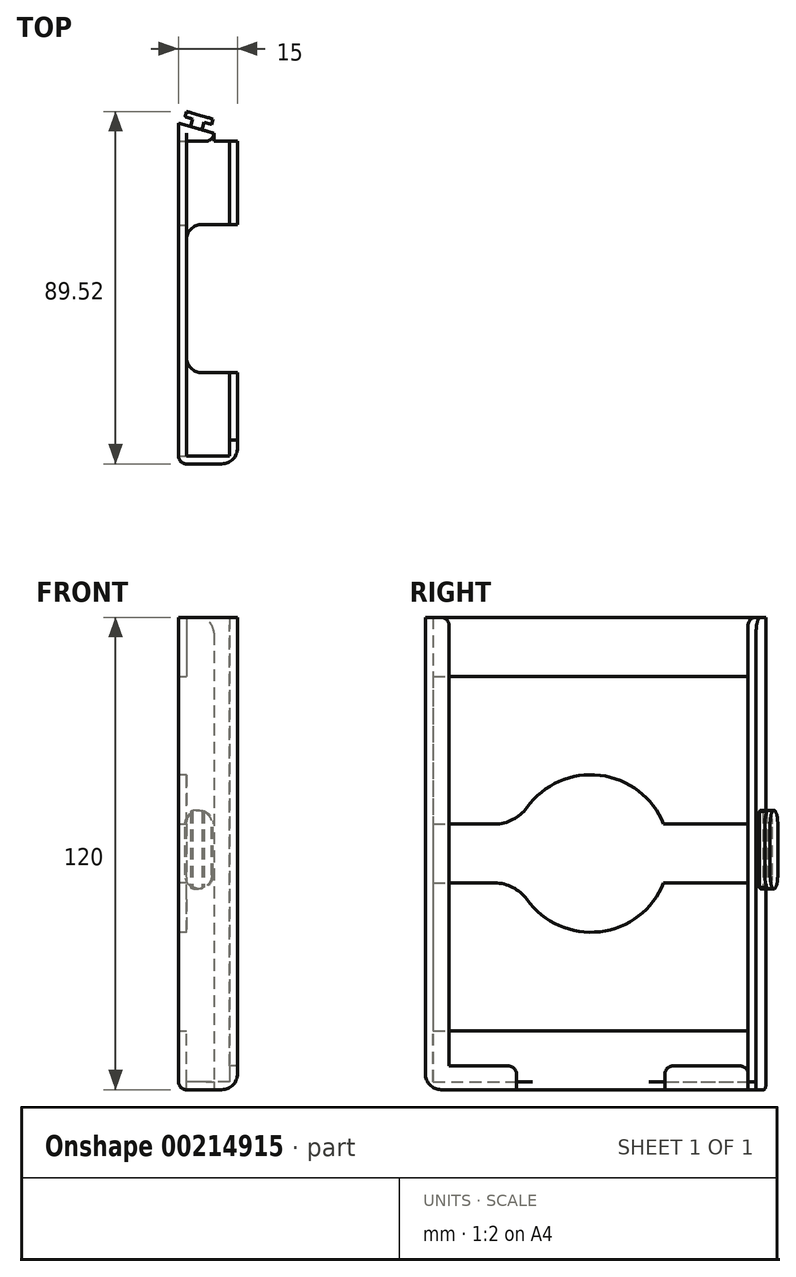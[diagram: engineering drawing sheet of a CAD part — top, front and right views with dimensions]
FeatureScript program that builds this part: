
annotation { "Feature Type Name" : "Feature", "Feature Type Description" : "" }
export const myFeature = defineFeature(function(context is Context, id is Id, definition is map)
    precondition{}
    {
        {
            var Q0;
            Q0=qCreatedBy(makeId("Front.planeOp"),FACE);
            var sketch = newSketch(context, id + "F0", { "sketchPlane" : qUnion([Q0])});
            skLineSegment(sketch, "E0.bottom", {"start": v(3.5, -10) * mm, "end": v(-3.5, -10) * mm});
            skLineSegment(sketch, "E0.top", {"start": v(3.5, 10) * mm, "end": v(-3.5, 10) * mm});
            skLineSegment(sketch, "E0.left", {"start": v(3.5, -10) * mm, "end": v(3.5, 10) * mm});
            skLineSegment(sketch, "E0.right", {"start": v(-3.5, -10) * mm, "end": v(-3.5, 10) * mm});
            skPoint(sketch, "E0.middle", {"position": v(0, 0) * mm});
            skSolve(sketch);
        }
        {
            var Q0;
            Q0=makeQuery(id+"F0.imprint","IMPRINT",FACE,{"disambiguationData":[TD([[makeQuery(id+"F0.imprint","IMPRINT",EDGE,{"derivedFrom":sQuery(id+"F0.wireOp",EDGE,"E0.bottom")}),-1.0]])]});
            extrude(context, id + "F1", {"entities" : qUnion([Q0]), "depth" : 1.4 * mm});
        }
        {
            var Q0;
            Q0=qCreatedBy(makeId("Front.planeOp"),FACE);
            var sketch = newSketch(context, id + "F2", { "sketchPlane" : qUnion([Q0])});
            skLineSegment(sketch, "E1.bottom", {"start": v(5.5, 60) * mm, "end": v(-3.5, 60) * mm});
            skLineSegment(sketch, "E1.top", {"start": v(5.5, -60) * mm, "end": v(-3.5, -60) * mm});
            skLineSegment(sketch, "E1.left", {"start": v(5.5, 60) * mm, "end": v(5.5, -60) * mm});
            skLineSegment(sketch, "E1.right", {"start": v(-3.5, 60) * mm, "end": v(-3.5, -60) * mm});
            skPoint(sketch, "E1.middle", {"position": v(1, 0) * mm});
            skSolve(sketch);
        }
        {
            var Q0;
            Q0=qSketchRegion(id+"F2",true);
            extrude(context, id + "F3", {"entities" : qUnion([Q0]), "operationType" : NewBodyOperationType.ADD, "depth" : 2 * mm});
        }
        {
            var Q0;
            Q0=makeQuery(id+"F11.boolean.opBoolean","MERGE",FACE,{"derivedFrom":[makeQuery(id+"F9.boolean.opBoolean","MERGE",FACE,{"derivedFrom":[makeQuery(id+"F7.boolean.opBoolean","MERGE",FACE,{"derivedFrom":[makeQuery(id+"F3.opExtrude","SWEPT_FACE",FACE,{"disambiguationData":[OSD([sQuery(id+"F2.wireOp",EDGE,"E1.top")])]}),makeQuery(id+"F7.opExtrude","SWEPT_FACE",FACE,{"disambiguationData":[OSD([sQuery(id+"F6.wireOp",EDGE,"E5.bottom")])]})]}),makeQuery(id+"F9.opExtrude","SWEPT_FACE",FACE,{"disambiguationData":[OSD([sQuery(id+"F8.wireOp",EDGE,"E8.top")])]})]}),makeQuery(id+"F11.opExtrude","SWEPT_FACE",FACE,{"disambiguationData":[OSD([sQuery(id+"F10.wireOp",EDGE,"E9.bottom")])]})]});
            var sketch = newSketch(context, id + "F4", { "sketchPlane" : qUnion([Q0])});
            skLineSegment(sketch, "E2", {"start": v(5.5, 0) * mm, "end": v(-3.5, -2.58) * mm});
            skLineSegment(sketch, "E3", {"start": v(-3.5, -2.58) * mm, "end": v(-3.5, 0) * mm});
            skSolve(sketch);
        }
        {
            var Q0;
            Q0 = qSketchRegion(id + "F4", true);
            var Q1;
            Q1=makeQuery(id+"F4.imprint","IMPRINT",FACE,{"disambiguationData":[TD([[makeQuery(id+"F4.imprint","IMPRINT",EDGE,{"derivedFrom":sQuery(id+"F4.wireOp",EDGE,"E2")}),-1.0]])]});
            var Q2;
            Q2=makeQuery(id+"F3.opExtrude","CAP_VERTEX",VERTEX,{"disambiguationData":[OSD([sQuery(id+"F2.wireOp",EDGE,"E1.bottom"),sQuery(id+"F2.wireOp",EDGE,"E1.right")])],"isStart":true});
            extrude(context, id + "F5", {"entities" : qUnion([Q0, Q1]), "operationType" : NewBodyOperationType.ADD, "endBound" : BoundingType.UP_TO_VERTEX, "oppositeDirection" : true, "endBoundEntityVertex" : qUnion([Q2]), "depth" : 25 * mm});
        }
        {
            var Q0;
            Q0=makeQuery(id+"F3.opExtrude","CAP_FACE",FACE,{"disambiguationData":[OSD([sQuery(id+"F2.wireOp",EDGE,"E1.bottom"),sQuery(id+"F2.wireOp",EDGE,"E1.top"),sQuery(id+"F2.wireOp",EDGE,"E1.left"),sQuery(id+"F2.wireOp",EDGE,"E1.right")])],"isStart":false});
            var sketch = newSketch(context, id + "F6", { "sketchPlane" : qUnion([Q0])});
            skLineSegment(sketch, "E4.bottom", {"start": v(-3.5, 60) * mm, "end": v(-1.5, 60) * mm});
            skLineSegment(sketch, "E4.top", {"start": v(-3.5, 45) * mm, "end": v(-1.5, 45) * mm});
            skLineSegment(sketch, "E4.left", {"start": v(-3.5, 60) * mm, "end": v(-3.5, 45) * mm});
            skLineSegment(sketch, "E4.right", {"start": v(-1.5, 60) * mm, "end": v(-1.5, 45) * mm});
            skLineSegment(sketch, "E5.bottom", {"start": v(-3.5, -60) * mm, "end": v(-1.5, -60) * mm});
            skLineSegment(sketch, "E5.top", {"start": v(-3.5, -45) * mm, "end": v(-1.5, -45) * mm});
            skLineSegment(sketch, "E5.left", {"start": v(-3.5, -60) * mm, "end": v(-3.5, -45) * mm});
            skLineSegment(sketch, "E5.right", {"start": v(-1.5, -60) * mm, "end": v(-1.5, -45) * mm});
            skLineSegment(sketch, "E6.bottom", {"start": v(-3.5, 7.5) * mm, "end": v(-1.5, 7.5) * mm});
            skLineSegment(sketch, "E6.top", {"start": v(-3.5, -7.5) * mm, "end": v(-1.5, -7.5) * mm});
            skLineSegment(sketch, "E6.left", {"start": v(-3.5, 7.5) * mm, "end": v(-3.5, -7.5) * mm});
            skLineSegment(sketch, "E6.right", {"start": v(-1.5, 7.5) * mm, "end": v(-1.5, -7.5) * mm});
            skPoint(sketch, "E7", {"position": v(-3.5, 0) * mm});
            skSolve(sketch);
        }
        {
            var Q0;
            Q0=qSketchRegion(id+"F6",true);
            extrude(context, id + "F7", {"entities" : qUnion([Q0]), "operationType" : NewBodyOperationType.ADD, "depth" : 80 * mm});
        }
        {
            var Q0;
            Q0=makeQuery(id+"F7.opExtrude","CAP_FACE",FACE,{"disambiguationData":[OSD([sQuery(id+"F6.wireOp",EDGE,"E4.bottom"),sQuery(id+"F6.wireOp",EDGE,"E4.top"),sQuery(id+"F6.wireOp",EDGE,"E4.left"),sQuery(id+"F6.wireOp",EDGE,"E4.right")])],"isStart":false});
            var sketch = newSketch(context, id + "F8", { "sketchPlane" : qUnion([Q0])});
            skLineSegment(sketch, "E8.bottom", {"start": v(-3.5, 60) * mm, "end": v(11.5, 60) * mm});
            skLineSegment(sketch, "E8.top", {"start": v(-3.5, -60) * mm, "end": v(11.5, -60) * mm});
            skLineSegment(sketch, "E8.left", {"start": v(-3.5, 60) * mm, "end": v(-3.5, -60) * mm});
            skLineSegment(sketch, "E8.right", {"start": v(11.5, 60) * mm, "end": v(11.5, -60) * mm});
            skSolve(sketch);
        }
        {
            var Q0;
            {var subQ2=sQuery(id+"F8.wireOp",EDGE,"E8.top");Q0=makeQuery(id+"F8.imprint","IMPRINT",FACE,{"disambiguationData":[TD([[makeQuery(id+"F8.imprint","IMPRINT",EDGE,{"derivedFrom":subQ2}),1.0]])]});}
            var Q1;
            {var subQ4=makeQuery(id+"F7.opExtrude","CAP_EDGE",EDGE,{"disambiguationData":[OSD([sQuery(id+"F6.wireOp",EDGE,"E4.top")])],"isStart":false});Q1=makeQuery(id+"F8.imprint","IMPRINT",FACE,{"disambiguationData":[TD([[makeQuery(id+"F8.imprint","IMPRINT",EDGE,{"derivedFrom":subQ4}),1.0]])]});}
            extrude(context, id + "F9", {"entities" : qUnion([Q0, Q1]), "operationType" : NewBodyOperationType.ADD, "depth" : 2 * mm});
        }
        {
            var Q0;
            Q0=makeQuery(id+"F7.opExtrude","SWEPT_FACE",FACE,{"disambiguationData":[OSD([sQuery(id+"F6.wireOp",EDGE,"E5.right")])]});
            var sketch = newSketch(context, id + "F10", { "sketchPlane" : qUnion([Q0])});
            skLineSegment(sketch, "E9.bottom", {"start": v(-82, -60) * mm, "end": v(-2, -60) * mm});
            skLineSegment(sketch, "E9.top", {"start": v(-82, -58) * mm, "end": v(-2, -58) * mm});
            skLineSegment(sketch, "E9.left", {"start": v(-82, -60) * mm, "end": v(-82, -58) * mm});
            skLineSegment(sketch, "E9.right", {"start": v(-2, -60) * mm, "end": v(-2, -58) * mm});
            skSolve(sketch);
        }
        {
            var Q0;
            Q0=makeQuery(id+"F10.imprint","IMPRINT",FACE,{"disambiguationData":[TD([[makeQuery(id+"F10.imprint","IMPRINT",EDGE,{"derivedFrom":sQuery(id+"F10.wireOp",EDGE,"E9.bottom")}),1.0]])]});
            var Q1;
            Q1=makeQuery(id+"F9.opExtrude","CAP_VERTEX",VERTEX,{"disambiguationData":[OSD([sQuery(id+"F8.wireOp",EDGE,"E8.top"),sQuery(id+"F8.wireOp",EDGE,"E8.right")])],"isStart":true});
            extrude(context, id + "F11", {"entities" : qUnion([Q0]), "operationType" : NewBodyOperationType.ADD, "endBound" : BoundingType.UP_TO_VERTEX, "endBoundEntityVertex" : qUnion([Q1]), "depth" : 25 * mm});
        }
        {
            var Q0;
            Q0=makeQuery(id+"F11.opExtrude","SWEPT_FACE",FACE,{"disambiguationData":[OSD([sQuery(id+"F10.wireOp",EDGE,"E9.top")])]});
            var sketch = newSketch(context, id + "F12", { "sketchPlane" : qUnion([Q0])});
            skLineSegment(sketch, "E10.bottom", {"start": v(11.5, -23.15) * mm, "end": v(-1.5, -23.15) * mm});
            skLineSegment(sketch, "E10.top", {"start": v(11.5, -60.85) * mm, "end": v(-1.5, -60.85) * mm});
            skLineSegment(sketch, "E10.left", {"start": v(11.5, -23.15) * mm, "end": v(11.5, -60.85) * mm});
            skLineSegment(sketch, "E10.right", {"start": v(-1.5, -23.15) * mm, "end": v(-1.5, -60.85) * mm});
            skPoint(sketch, "E10.middle", {"position": v(5, -42) * mm});
            skPoint(sketch, "E10.middle.positionSnap0", {"position": v(5, -82) * mm});
            skPoint(sketch, "E10.middle.positionSnap1", {"position": v(-1.5, -42) * mm});
            skPoint(sketch, "E10.centerSnap0", {"position": v(5, -82) * mm});
            skPoint(sketch, "E10.centerSnap1", {"position": v(-1.5, -42) * mm});
            skSolve(sketch);
        }
        {
            var Q0;
            Q0=makeQuery(id+"F12.imprint","IMPRINT",FACE,{"disambiguationData":[TD([[makeQuery(id+"F12.imprint","IMPRINT",EDGE,{"derivedFrom":sQuery(id+"F12.wireOp",EDGE,"E10.bottom")}),1.0]])]});
            extrude(context, id + "F13", {"entities" : qUnion([Q0]), "operationType" : NewBodyOperationType.REMOVE, "endBound" : BoundingType.THROUGH_ALL, "oppositeDirection" : true, "depth" : 25 * mm});
        }
        {
            var Q0;
            Q0=makeQuery(id+"F13.boolean.opBoolean","SPLIT",FACE,{"disambiguationData":[TD([makeQuery(id+"F13.opExtrude","SWEPT_FACE",FACE,{"disambiguationData":[OSD([sQuery(id+"F12.wireOp",EDGE,"E10.top")])]})])],"derivedFrom":makeQuery(id+"F11.opExtrude","SWEPT_FACE",FACE,{"disambiguationData":[OSD([sQuery(id+"F10.wireOp",EDGE,"E9.top")])]})});
            var sketch = newSketch(context, id + "F14", { "sketchPlane" : qUnion([Q0])});
            skLineSegment(sketch, "E11.bottom", {"start": v(11.5, -82) * mm, "end": v(9.5, -82) * mm});
            skLineSegment(sketch, "E11.top", {"start": v(11.5, -60.85) * mm, "end": v(9.5, -60.85) * mm});
            skLineSegment(sketch, "E11.left", {"start": v(11.5, -82) * mm, "end": v(11.5, -60.85) * mm});
            skLineSegment(sketch, "E11.right", {"start": v(9.5, -82) * mm, "end": v(9.5, -60.85) * mm});
            skSolve(sketch);
        }
        {
            var Q0;
            {var subQ0=sQuery(id+"F2.wireOp",EDGE,"E1.left");Q0=makeQuery(id+"F13.boolean.opBoolean","SPLIT",FACE,{"disambiguationData":[TD([makeQuery(id+"F3.opExtrude","SWEPT_FACE",FACE,{"disambiguationData":[OSD([subQ0])]})])],"derivedFrom":makeQuery(id+"F11.opExtrude","SWEPT_FACE",FACE,{"disambiguationData":[OSD([sQuery(id+"F10.wireOp",EDGE,"E9.top")])]})});}
            var sketch = newSketch(context, id + "F15", { "sketchPlane" : qUnion([Q0])});
            skLineSegment(sketch, "E12.bottom", {"start": v(11.5, -23.15) * mm, "end": v(9.5, -23.15) * mm});
            skLineSegment(sketch, "E12.top", {"start": v(11.5, -2) * mm, "end": v(9.5, -2) * mm});
            skLineSegment(sketch, "E12.left", {"start": v(11.5, -23.15) * mm, "end": v(11.5, -2) * mm});
            skLineSegment(sketch, "E12.right", {"start": v(9.5, -23.15) * mm, "end": v(9.5, -2) * mm});
            skSolve(sketch);
        }
        {
            var Q0;
            Q0=makeQuery(id+"F14.imprint","IMPRINT",FACE,{"disambiguationData":[TD([[makeQuery(id+"F14.imprint","IMPRINT",EDGE,{"derivedFrom":sQuery(id+"F14.wireOp",EDGE,"E11.bottom")}),-1.0]])]});
            var Q1;
            Q1=makeQuery(id+"F15.imprint","IMPRINT",FACE,{"disambiguationData":[TD([[makeQuery(id+"F15.imprint","IMPRINT",EDGE,{"derivedFrom":sQuery(id+"F15.wireOp",EDGE,"E12.bottom")}),-1.0]])]});
            extrude(context, id + "F16", {"entities" : qUnion([Q0, Q1]), "operationType" : NewBodyOperationType.ADD, "depth" : 4 * mm});
        }
        {
            var Q0;
            Q0=makeQuery(id+"F9.opExtrude","CAP_FACE",FACE,{"disambiguationData":[OSD([sQuery(id+"F8.wireOp",EDGE,"E8.bottom"),sQuery(id+"F8.wireOp",EDGE,"E8.top"),sQuery(id+"F8.wireOp",EDGE,"E8.left"),sQuery(id+"F8.wireOp",EDGE,"E8.right")])],"isStart":true});
            var sketch = newSketch(context, id + "F17", { "sketchPlane" : qUnion([Q0])});
            skLineSegment(sketch, "E13.bottom", {"start": v(-11.5, -54) * mm, "end": v(-9.5, -54) * mm});
            skLineSegment(sketch, "E13.top", {"start": v(-11.5, 60) * mm, "end": v(-9.5, 60) * mm});
            skLineSegment(sketch, "E13.left", {"start": v(-11.5, -54) * mm, "end": v(-11.5, 60) * mm});
            skLineSegment(sketch, "E13.right", {"start": v(-9.5, -54) * mm, "end": v(-9.5, 60) * mm});
            skSolve(sketch);
        }
        {
            var Q0;
            Q0=makeQuery(id+"F17.imprint","IMPRINT",FACE,{"disambiguationData":[TD([[makeQuery(id+"F17.imprint","IMPRINT",EDGE,{"derivedFrom":sQuery(id+"F17.wireOp",EDGE,"E13.bottom")}),1.0]])]});
            extrude(context, id + "F18", {"entities" : qUnion([Q0]), "operationType" : NewBodyOperationType.ADD, "depth" : 4 * mm});
        }
        {
            var Q0;
            {var subQ0=sQuery(id+"F8.wireOp",EDGE,"E8.right");var subQ1=dummyQuery(id+"F11.vertexPlane.planeOp",FACE);var subQ2=sQuery(id+"F8.wireOp",EDGE,"E8.top");var subQ3=sQuery(id+"F10.wireOp",EDGE,"E9.bottom");Q0=makeQuery(id+"F13.boolean.opBoolean","SPLIT",EDGE,{"disambiguationData":[TD([makeQuery(id+"F11.opExtrude","SWEPT_FACE",FACE,{"disambiguationData":[OSD([sQuery(id+"F10.wireOp",EDGE,"E9.right")])]})])],"derivedFrom":makeQuery(id+"F11.boolean.opBoolean","MERGE",EDGE,{"derivedFrom":[makeQuery(id+"F9.opExtrude","SWEPT_EDGE",EDGE,{"disambiguationData":[OSD([subQ2,subQ0])]}),makeQuery(id+"F11.opExtrude","TWEAK_EDGE",EDGE,{"derivedFrom":[makeQuery(id+"F10.imprint","IMPRINT",EDGE,{"derivedFrom":subQ3}),subQ1]})]})});}
            var Q1;
            {var subQ0=sQuery(id+"F8.wireOp",EDGE,"E8.top");var subQ1=sQuery(id+"F10.wireOp",EDGE,"E9.bottom");var subQ2=sQuery(id+"F8.wireOp",EDGE,"E8.right");var subQ3=dummyQuery(id+"F11.vertexPlane.planeOp",FACE);Q1=makeQuery(id+"F13.boolean.opBoolean","SPLIT",EDGE,{"disambiguationData":[TD([makeQuery(id+"F13.opExtrude","SWEPT_FACE",FACE,{"disambiguationData":[OSD([sQuery(id+"F12.wireOp",EDGE,"E10.top")])]})])],"derivedFrom":makeQuery(id+"F11.boolean.opBoolean","MERGE",EDGE,{"derivedFrom":[makeQuery(id+"F9.opExtrude","SWEPT_EDGE",EDGE,{"disambiguationData":[OSD([subQ0,subQ2])]}),makeQuery(id+"F11.opExtrude","TWEAK_EDGE",EDGE,{"derivedFrom":[makeQuery(id+"F10.imprint","IMPRINT",EDGE,{"derivedFrom":subQ1}),subQ3]})]})});}
            var Q2;
            Q2=makeQuery(id+"F9.opExtrude","CAP_EDGE",EDGE,{"disambiguationData":[OSD([sQuery(id+"F8.wireOp",EDGE,"E8.right")])],"isStart":false});
            var Q3;
            Q3=makeQuery(id+"F16.opExtrude","CAP_EDGE",EDGE,{"disambiguationData":[OSD([sQuery(id+"F14.wireOp",EDGE,"E11.right")])],"isStart":true});
            var Q4;
            Q4=makeQuery(id+"F18.boolean.opBoolean","MERGE",EDGE,{"derivedFrom":[makeQuery(id+"F16.opExtrude","SWEPT_EDGE",EDGE,{"disambiguationData":[OSD([sQuery(id+"F6.wireOp",EDGE,"E5.right"),sQuery(id+"F10.wireOp",EDGE,"E9.top"),sQuery(id+"F10.wireOp",EDGE,"E9.left"),sQuery(id+"F14.wireOp",EDGE,"E11.bottom"),sQuery(id+"F14.wireOp",EDGE,"E11.right")])]}),makeQuery(id+"F18.opExtrude","CAP_EDGE",EDGE,{"disambiguationData":[OSD([sQuery(id+"F17.wireOp",EDGE,"E13.right")])],"isStart":true})]});
            var Q5;
            Q5=makeQuery(id+"F16.opExtrude","CAP_EDGE",EDGE,{"disambiguationData":[OSD([sQuery(id+"F15.wireOp",EDGE,"E12.right")])],"isStart":true});
            var Q6;
            Q6=makeQuery(id+"F3.opExtrude","SWEPT_EDGE",EDGE,{"disambiguationData":[OSD([sQuery(id+"F2.wireOp",EDGE,"E1.bottom"),sQuery(id+"F2.wireOp",EDGE,"E1.left")])]});
            var Q7;
            Q7=makeQuery(id+"F9.opExtrude","CAP_EDGE",EDGE,{"disambiguationData":[OSD([sQuery(id+"F8.wireOp",EDGE,"E8.top")])],"isStart":false});
            var Q8;
            Q8=makeQuery(id+"F11.opExtrude","SWEPT_EDGE",EDGE,{"disambiguationData":[OSD([sQuery(id+"F6.wireOp",EDGE,"E5.right"),sQuery(id+"F10.wireOp",EDGE,"E9.top"),sQuery(id+"F10.wireOp",EDGE,"E9.left")])]});
            var Q9;
            Q9=makeQuery(id+"F13.boolean.opBoolean","COPY",EDGE,{"derivedFrom":makeQuery(id+"F13.opExtrude","SWEPT_EDGE",EDGE,{"disambiguationData":[OSD([sQuery(id+"F10.wireOp",EDGE,"E9.top"),sQuery(id+"F12.wireOp",EDGE,"E10.bottom"),sQuery(id+"F12.wireOp",EDGE,"E10.right")])]})});
            var Q10;
            Q10=makeQuery(id+"F13.boolean.opBoolean","COPY",EDGE,{"derivedFrom":makeQuery(id+"F13.opExtrude","SWEPT_EDGE",EDGE,{"disambiguationData":[OSD([sQuery(id+"F10.wireOp",EDGE,"E9.top"),sQuery(id+"F12.wireOp",EDGE,"E10.top"),sQuery(id+"F12.wireOp",EDGE,"E10.right")])]})});
            var Q11;
            Q11=makeQuery(id+"F7.opExtrude","CAP_EDGE",EDGE,{"disambiguationData":[OSD([sQuery(id+"F6.wireOp",EDGE,"E6.top")])],"isStart":true});
            var Q12;
            Q12=makeQuery(id+"F7.opExtrude","CAP_EDGE",EDGE,{"disambiguationData":[OSD([sQuery(id+"F6.wireOp",EDGE,"E6.top")])],"isStart":false});
            var Q13;
            Q13=makeQuery(id+"F7.opExtrude","CAP_EDGE",EDGE,{"disambiguationData":[OSD([sQuery(id+"F6.wireOp",EDGE,"E5.top")])],"isStart":false});
            var Q14;
            Q14=makeQuery(id+"F7.opExtrude","CAP_EDGE",EDGE,{"disambiguationData":[OSD([sQuery(id+"F6.wireOp",EDGE,"E5.top")])],"isStart":true});
            var Q15;
            Q15=makeQuery(id+"F7.opExtrude","CAP_EDGE",EDGE,{"disambiguationData":[OSD([sQuery(id+"F6.wireOp",EDGE,"E4.top")])],"isStart":false});
            var Q16;
            Q16=makeQuery(id+"F7.opExtrude","CAP_EDGE",EDGE,{"disambiguationData":[OSD([sQuery(id+"F6.wireOp",EDGE,"E4.top")])],"isStart":true});
            var Q17;
            Q17=makeQuery(id+"F7.opExtrude","CAP_EDGE",EDGE,{"disambiguationData":[OSD([sQuery(id+"F6.wireOp",EDGE,"E6.bottom")])],"isStart":false});
            var Q18;
            Q18=makeQuery(id+"F7.opExtrude","CAP_EDGE",EDGE,{"disambiguationData":[OSD([sQuery(id+"F6.wireOp",EDGE,"E6.bottom")])],"isStart":true});
            fillet(context, id + "F19", {"entities" : qUnion([Q0, Q1, Q2, Q3, Q4, Q5, Q6, Q7, Q8, Q9, Q10, Q11, Q12, Q13, Q14, Q15, Q16, Q17, Q18]), "radius" : 4 * mm, "tangentPropagation" : true, "allowEdgeOverflow" : false});
        }
        {
            var Q0;
            {var subQ0=sQuery(id+"F2.wireOp",EDGE,"E1.top");var subQ1=sQuery(id+"F2.wireOp",EDGE,"E1.left");Q0=makeQuery(id+"F11.boolean.opBoolean","SPLIT",EDGE,{"disambiguationData":[TD([makeQuery(id+"F3.opExtrude","SWEPT_FACE",FACE,{"disambiguationData":[OSD([subQ0])]})])],"derivedFrom":makeQuery(id+"F3.opExtrude","CAP_EDGE",EDGE,{"disambiguationData":[OSD([subQ1])],"isStart":false})});}
            var Q1;
            Q1=makeQuery(id+"F16.opExtrude","CAP_EDGE",EDGE,{"disambiguationData":[OSD([sQuery(id+"F15.wireOp",EDGE,"E12.bottom")])],"isStart":false});
            var Q2;
            Q2=makeQuery(id+"F16.opExtrude","CAP_EDGE",EDGE,{"disambiguationData":[OSD([sQuery(id+"F15.wireOp",EDGE,"E12.top")])],"isStart":false});
            var Q3;
            Q3=makeQuery(id+"F16.opExtrude","CAP_EDGE",EDGE,{"disambiguationData":[OSD([sQuery(id+"F14.wireOp",EDGE,"E11.top")])],"isStart":false});
            var Q4;
            Q4=makeQuery(id+"F18.opExtrude","CAP_EDGE",EDGE,{"disambiguationData":[OSD([sQuery(id+"F17.wireOp",EDGE,"E13.bottom")])],"isStart":false});
            var Q5;
            Q5=makeQuery(id+"F18.opExtrude","CAP_EDGE",EDGE,{"disambiguationData":[OSD([sQuery(id+"F17.wireOp",EDGE,"E13.top")])],"isStart":false});
            var Q6;
            Q6=makeQuery(id+"F7.opExtrude","CAP_EDGE",EDGE,{"disambiguationData":[OSD([sQuery(id+"F6.wireOp",EDGE,"E4.right")])],"isStart":false});
            var Q7;
            Q7=makeQuery(id+"F7.opExtrude","CAP_EDGE",EDGE,{"disambiguationData":[OSD([sQuery(id+"F6.wireOp",EDGE,"E6.right")])],"isStart":false});
            var Q8;
            Q8=makeQuery(id+"F7.opExtrude","CAP_EDGE",EDGE,{"disambiguationData":[OSD([sQuery(id+"F6.wireOp",EDGE,"E5.right")])],"isStart":false});
            var Q9;
            {var subQ0=sQuery(id+"F10.wireOp",EDGE,"E9.top");Q9=makeQuery(id+"F13.boolean.opBoolean","SPLIT",EDGE,{"disambiguationData":[TD([makeQuery(id+"F13.opExtrude","SWEPT_FACE",FACE,{"disambiguationData":[OSD([sQuery(id+"F12.wireOp",EDGE,"E10.bottom")])]})])],"derivedFrom":makeQuery(id+"F11.opExtrude","CAP_EDGE",EDGE,{"disambiguationData":[OSD([subQ0])],"isStart":true})});}
            var Q10;
            Q10=makeQuery(id+"F7.opExtrude","CAP_EDGE",EDGE,{"disambiguationData":[OSD([sQuery(id+"F6.wireOp",EDGE,"E5.right")])],"isStart":true});
            var Q11;
            Q11=makeQuery(id+"F7.opExtrude","CAP_EDGE",EDGE,{"disambiguationData":[OSD([sQuery(id+"F6.wireOp",EDGE,"E6.right")])],"isStart":true});
            var Q12;
            Q12=makeQuery(id+"F7.opExtrude","CAP_EDGE",EDGE,{"disambiguationData":[OSD([sQuery(id+"F6.wireOp",EDGE,"E4.right")])],"isStart":true});
            var Q13;
            Q13=makeQuery(id+"F9.opExtrude","CAP_EDGE",EDGE,{"disambiguationData":[OSD([sQuery(id+"F8.wireOp",EDGE,"E8.left")])],"isStart":false});
            fillet(context, id + "F20", {"entities" : qUnion([Q0, Q1, Q2, Q3, Q4, Q5, Q6, Q7, Q8, Q9, Q10, Q11, Q12, Q13]), "radius" : 2 * mm, "tangentPropagation" : true, "allowEdgeOverflow" : false});
        }
        {
            var Q0;
            Q0=makeQuery(id+"F5.opExtrude","SWEPT_FACE",FACE,{"disambiguationData":[OSD([sQuery(id+"F4.wireOp",EDGE,"E2")])]});
            var sketch = newSketch(context, id + "F21", { "sketchPlane" : qUnion([Q0])});
            skLineSegment(sketch, "E14.bottom", {"start": v(0.9, 11) * mm, "end": v(-2.1, 11) * mm});
            skLineSegment(sketch, "E14.top", {"start": v(0.9, -9) * mm, "end": v(-2.1, -9) * mm});
            skLineSegment(sketch, "E14.left", {"start": v(0.9, 11) * mm, "end": v(0.9, -9) * mm});
            skLineSegment(sketch, "E14.right", {"start": v(-2.1, 11) * mm, "end": v(-2.1, -9) * mm});
            skPoint(sketch, "E14.middle", {"position": v(-0.6, 1) * mm});
            skLineSegment(sketch, "E15", {"start": v(4.08, 1) * mm, "end": v(-5.29, 1) * mm, "construction": true});
            skPoint(sketch, "E15.endSnap0", {"position": v(-5.29, -1) * mm});
            skSolve(sketch);
        }
        {
            var Q0;
            Q0=makeQuery(id+"F21.imprint","IMPRINT",FACE,{"disambiguationData":[TD([[makeQuery(id+"F21.imprint","IMPRINT",EDGE,{"derivedFrom":sQuery(id+"F21.wireOp",EDGE,"E14.bottom")}),1.0]])]});
            extrude(context, id + "F22", {"entities" : qUnion([Q0]), "operationType" : NewBodyOperationType.ADD, "depth" : 2 * mm});
        }
        {
            var Q0;
            Q0=makeQuery(id+"F22.opExtrude","CAP_FACE",FACE,{"disambiguationData":[OSD([sQuery(id+"F21.wireOp",EDGE,"E14.bottom"),sQuery(id+"F21.wireOp",EDGE,"E14.top"),sQuery(id+"F21.wireOp",EDGE,"E14.left"),sQuery(id+"F21.wireOp",EDGE,"E14.right")])],"isStart":false});
            var sketch = newSketch(context, id + "F23", { "sketchPlane" : qUnion([Q0])});
            skLineSegment(sketch, "E16.bottom", {"start": v(2.9, -9) * mm, "end": v(-4.1, -9) * mm});
            skLineSegment(sketch, "E16.top", {"start": v(2.9, 11) * mm, "end": v(-4.1, 11) * mm});
            skLineSegment(sketch, "E16.left", {"start": v(2.9, -9) * mm, "end": v(2.9, 11) * mm});
            skLineSegment(sketch, "E16.right", {"start": v(-4.1, -9) * mm, "end": v(-4.1, 11) * mm});
            skPoint(sketch, "E16.middle", {"position": v(-0.6, 1) * mm});
            skLineSegment(sketch, "E17", {"start": v(0.9, 1) * mm, "end": v(-2.1, 1) * mm, "construction": true});
            skSolve(sketch);
        }
        {
            var Q0;
            Q0 = qSketchRegion(id + "F23", true);
            extrude(context, id + "F24", {"entities" : qUnion([Q0]), "operationType" : NewBodyOperationType.ADD, "depth" : 1.4 * mm});
        }
        {
            var Q0;
            Q0=makeQuery(id+"F24.opExtrude","SWEPT_EDGE",EDGE,{"disambiguationData":[OSD([sQuery(id+"F23.wireOp",EDGE,"E16.bottom"),sQuery(id+"F23.wireOp",EDGE,"E16.right")])]});
            var Q1;
            Q1=makeQuery(id+"F24.opExtrude","SWEPT_EDGE",EDGE,{"disambiguationData":[OSD([sQuery(id+"F23.wireOp",EDGE,"E16.bottom"),sQuery(id+"F23.wireOp",EDGE,"E16.left")])]});
            var Q2;
            Q2=makeQuery(id+"F24.opExtrude","SWEPT_EDGE",EDGE,{"disambiguationData":[OSD([sQuery(id+"F23.wireOp",EDGE,"E16.top"),sQuery(id+"F23.wireOp",EDGE,"E16.right")])]});
            var Q3;
            Q3=makeQuery(id+"F24.opExtrude","SWEPT_EDGE",EDGE,{"disambiguationData":[OSD([sQuery(id+"F23.wireOp",EDGE,"E16.top"),sQuery(id+"F23.wireOp",EDGE,"E16.left")])]});
            fillet(context, id + "F25", {"entities" : qUnion([Q0, Q1, Q2, Q3]), "radius" : 3.5 * mm, "tangentPropagation" : true, "allowEdgeOverflow" : false});
        }
        {
            var Q0;
            Q0=makeQuery(id+"F9.boolean.opBoolean","MERGE",FACE,{"derivedFrom":[makeQuery(id+"F7.boolean.opBoolean","MERGE",FACE,{"derivedFrom":[makeQuery(id+"F5.boolean.opBoolean","MERGE",FACE,{"derivedFrom":[makeQuery(id+"F3.boolean.opBoolean","MERGE",FACE,{"derivedFrom":[makeQuery(id+"F1.opExtrude","SWEPT_FACE",FACE,{"disambiguationData":[OSD([sQuery(id+"F0.wireOp",EDGE,"E0.right")])]}),makeQuery(id+"F3.opExtrude","SWEPT_FACE",FACE,{"disambiguationData":[OSD([sQuery(id+"F2.wireOp",EDGE,"E1.right")])]})]}),makeQuery(id+"F5.opExtrude","SWEPT_FACE",FACE,{"disambiguationData":[OSD([sQuery(id+"F4.wireOp",EDGE,"E3")])]})]}),makeQuery(id+"F7.opExtrude","SWEPT_FACE",FACE,{"disambiguationData":[OSD([sQuery(id+"F6.wireOp",EDGE,"E4.left")])]}),makeQuery(id+"F7.opExtrude","SWEPT_FACE",FACE,{"disambiguationData":[OSD([sQuery(id+"F6.wireOp",EDGE,"E5.left")])]}),makeQuery(id+"F7.opExtrude","SWEPT_FACE",FACE,{"disambiguationData":[OSD([sQuery(id+"F6.wireOp",EDGE,"E6.left")])]})]}),makeQuery(id+"F9.opExtrude","SWEPT_FACE",FACE,{"disambiguationData":[OSD([sQuery(id+"F8.wireOp",EDGE,"E8.left")])]})]});
            var sketch = newSketch(context, id + "F26", { "sketchPlane" : qUnion([Q0])});
            skCircle(sketch, "E18", {"center": v(42, 0) * mm, "radius": 20 * mm});
            skPoint(sketch, "E18.centerSnap0", {"position": v(42, -7.5) * mm});
            skSolve(sketch);
        }
        {
            var Q0;
            {var subQ0=sQuery(id+"F26.wireOp",EDGE,"E18");var subQ1=makeQuery(id+"F7.opExtrude","SWEPT_EDGE",EDGE,{"disambiguationData":[OSD([sQuery(id+"F2.wireOp",EDGE,"E1.right"),sQuery(id+"F6.wireOp",EDGE,"E6.top"),sQuery(id+"F6.wireOp",EDGE,"E6.left")])]});var subQ2=makeQuery(id+"F26.imprint","INTERSECT",VERTEX,{"disambiguationData":[OD(0.0)],"derivedFrom":[subQ1,subQ0]});Q0=makeQuery(id+"F26.imprint","IMPRINT",FACE,{"disambiguationData":[TD([[makeQuery(id+"F26.imprint","IMPRINT",EDGE,{"disambiguationData":[TD([[subQ2,-1.0]])],"derivedFrom":subQ0}),1.0]])]});}
            var Q1;
            {var subQ0=sQuery(id+"F26.wireOp",EDGE,"E18");var subQ1=makeQuery(id+"F7.opExtrude","SWEPT_EDGE",EDGE,{"disambiguationData":[OSD([sQuery(id+"F2.wireOp",EDGE,"E1.right"),sQuery(id+"F6.wireOp",EDGE,"E6.bottom"),sQuery(id+"F6.wireOp",EDGE,"E6.left")])]});var subQ2=makeQuery(id+"F26.imprint","INTERSECT",VERTEX,{"disambiguationData":[OD(0.0)],"derivedFrom":[subQ1,subQ0]});Q1=makeQuery(id+"F26.imprint","IMPRINT",FACE,{"disambiguationData":[TD([[makeQuery(id+"F26.imprint","IMPRINT",EDGE,{"disambiguationData":[TD([[subQ2,1.0]])],"derivedFrom":subQ0}),1.0]])]});}
            var Q2;
            Q2=makeQuery(id+"F7.opExtrude","SWEPT_FACE",FACE,{"disambiguationData":[OSD([sQuery(id+"F6.wireOp",EDGE,"E6.right")])]});
            extrude(context, id + "F27", {"entities" : qUnion([Q0, Q1]), "operationType" : NewBodyOperationType.ADD, "endBound" : BoundingType.UP_TO_SURFACE, "oppositeDirection" : true, "endBoundEntityFace" : qUnion([Q2]), "depth" : 25 * mm});
        }
        {
            var Q0;
            {var subQ0=sQuery(id+"F26.wireOp",EDGE,"E18");var subQ1=sQuery(id+"F6.wireOp",EDGE,"E6.left");var subQ2=sQuery(id+"F6.wireOp",EDGE,"E6.bottom");var subQ3=sQuery(id+"F2.wireOp",EDGE,"E1.right");Q0=makeQuery(id+"F27.opExtrude","SWEPT_EDGE",EDGE,{"disambiguationData":[OSD([subQ3,subQ2,subQ1,subQ0]),TDD([makeQuery(id+"F26.imprint","INTERSECT",VERTEX,{"disambiguationData":[OD(1.0)],"derivedFrom":[makeQuery(id+"F7.opExtrude","SWEPT_EDGE",EDGE,{"disambiguationData":[OSD([subQ3,subQ2,subQ1])]}),subQ0]})])]});}
            var Q1;
            {var subQ0=sQuery(id+"F26.wireOp",EDGE,"E18");var subQ1=sQuery(id+"F6.wireOp",EDGE,"E6.left");var subQ2=sQuery(id+"F6.wireOp",EDGE,"E6.top");var subQ3=sQuery(id+"F2.wireOp",EDGE,"E1.right");Q1=makeQuery(id+"F27.opExtrude","SWEPT_EDGE",EDGE,{"disambiguationData":[OSD([subQ3,subQ2,subQ1,subQ0]),TDD([makeQuery(id+"F26.imprint","INTERSECT",VERTEX,{"disambiguationData":[OD(1.0)],"derivedFrom":[makeQuery(id+"F7.opExtrude","SWEPT_EDGE",EDGE,{"disambiguationData":[OSD([subQ3,subQ2,subQ1])]}),subQ0]})])]});}
            var Q2;
            {var subQ0=sQuery(id+"F26.wireOp",EDGE,"E18");var subQ1=sQuery(id+"F6.wireOp",EDGE,"E6.left");var subQ2=sQuery(id+"F6.wireOp",EDGE,"E6.top");var subQ3=sQuery(id+"F2.wireOp",EDGE,"E1.right");Q2=makeQuery(id+"F27.opExtrude","SWEPT_EDGE",EDGE,{"disambiguationData":[OSD([subQ3,subQ2,subQ1,subQ0]),TDD([makeQuery(id+"F26.imprint","INTERSECT",VERTEX,{"disambiguationData":[OD(0.0)],"derivedFrom":[makeQuery(id+"F7.opExtrude","SWEPT_EDGE",EDGE,{"disambiguationData":[OSD([subQ3,subQ2,subQ1])]}),subQ0]})])]});}
            var Q3;
            {var subQ0=sQuery(id+"F26.wireOp",EDGE,"E18");var subQ1=sQuery(id+"F6.wireOp",EDGE,"E6.left");var subQ2=sQuery(id+"F6.wireOp",EDGE,"E6.bottom");var subQ3=sQuery(id+"F2.wireOp",EDGE,"E1.right");Q3=makeQuery(id+"F27.opExtrude","SWEPT_EDGE",EDGE,{"disambiguationData":[OSD([subQ3,subQ2,subQ1,subQ0]),TDD([makeQuery(id+"F26.imprint","INTERSECT",VERTEX,{"disambiguationData":[OD(0.0)],"derivedFrom":[makeQuery(id+"F7.opExtrude","SWEPT_EDGE",EDGE,{"disambiguationData":[OSD([subQ3,subQ2,subQ1])]}),subQ0]})])]});}
            fillet(context, id + "F28", {"entities" : qUnion([Q0, Q1, Q2, Q3]), "radius" : 10 * mm, "tangentPropagation" : true, "allowEdgeOverflow" : false});
        }
    });
